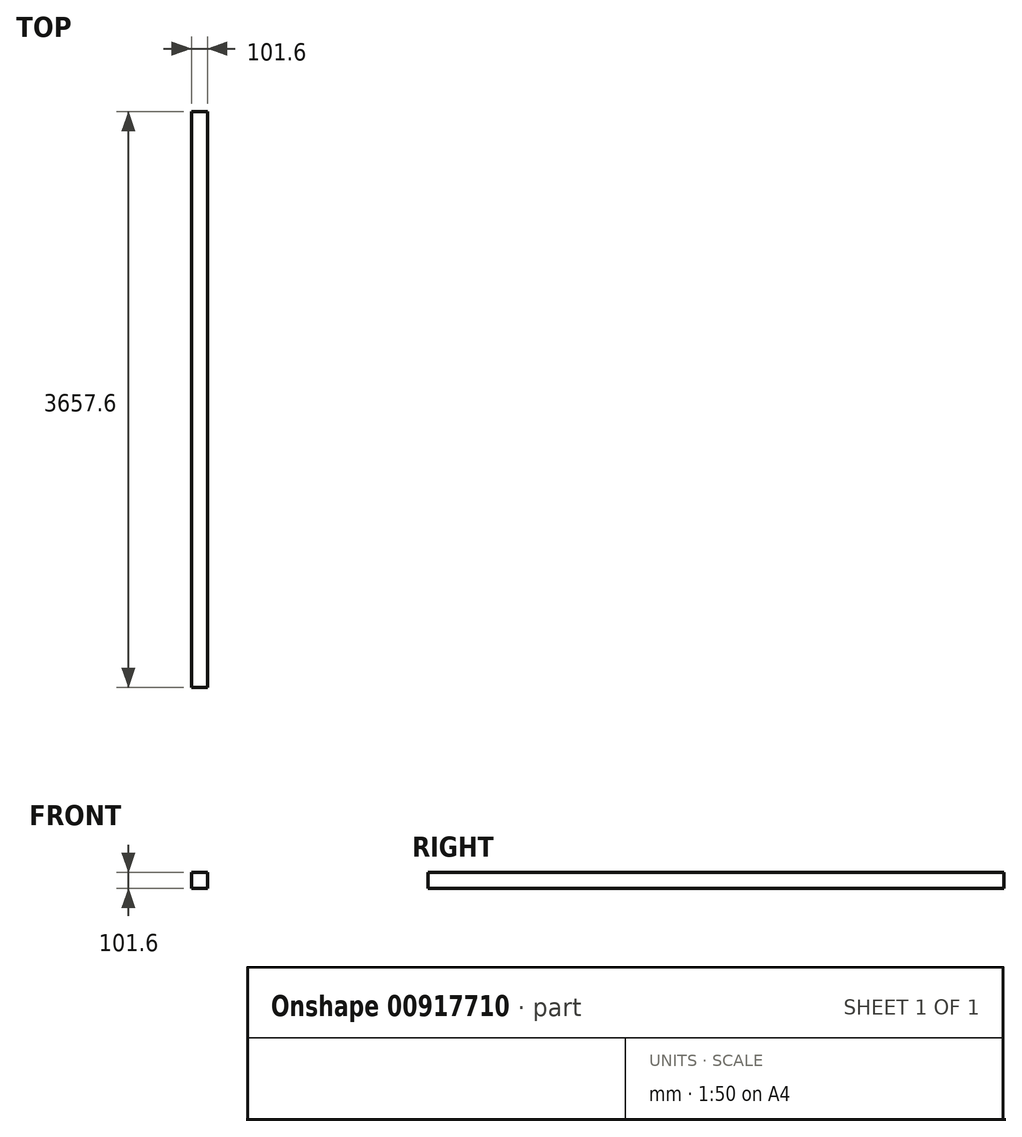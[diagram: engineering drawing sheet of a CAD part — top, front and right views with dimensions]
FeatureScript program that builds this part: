
annotation { "Feature Type Name" : "Feature", "Feature Type Description" : "" }
export const myFeature = defineFeature(function(context is Context, id is Id, definition is map)
    precondition{}
    {
        {
            var Q0;
            Q0=qCreatedBy(makeId("Front.planeOp"),FACE);
            var sketch = newSketch(context, id + "F0", { "sketchPlane" : qUnion([Q0])});
            skLineSegment(sketch, "E0.bottom", {"start": v(0, 0) * mm, "end": v(-101.6, 0) * mm});
            skLineSegment(sketch, "E0.top", {"start": v(0, 101.6) * mm, "end": v(-101.6, 101.6) * mm});
            skLineSegment(sketch, "E0.left", {"start": v(0, 0) * mm, "end": v(0, 101.6) * mm});
            skLineSegment(sketch, "E0.right", {"start": v(-101.6, 0) * mm, "end": v(-101.6, 101.6) * mm});
            skSolve(sketch);
        }
        {
            var Q0;
            Q0 = qSketchRegion(id + "F0", true);
            extrude(context, id + "F1", {"entities" : qUnion([Q0]), "depth" : 3657.6 * mm, "offsetDistance" : 25.4 * mm});
        }
    });
